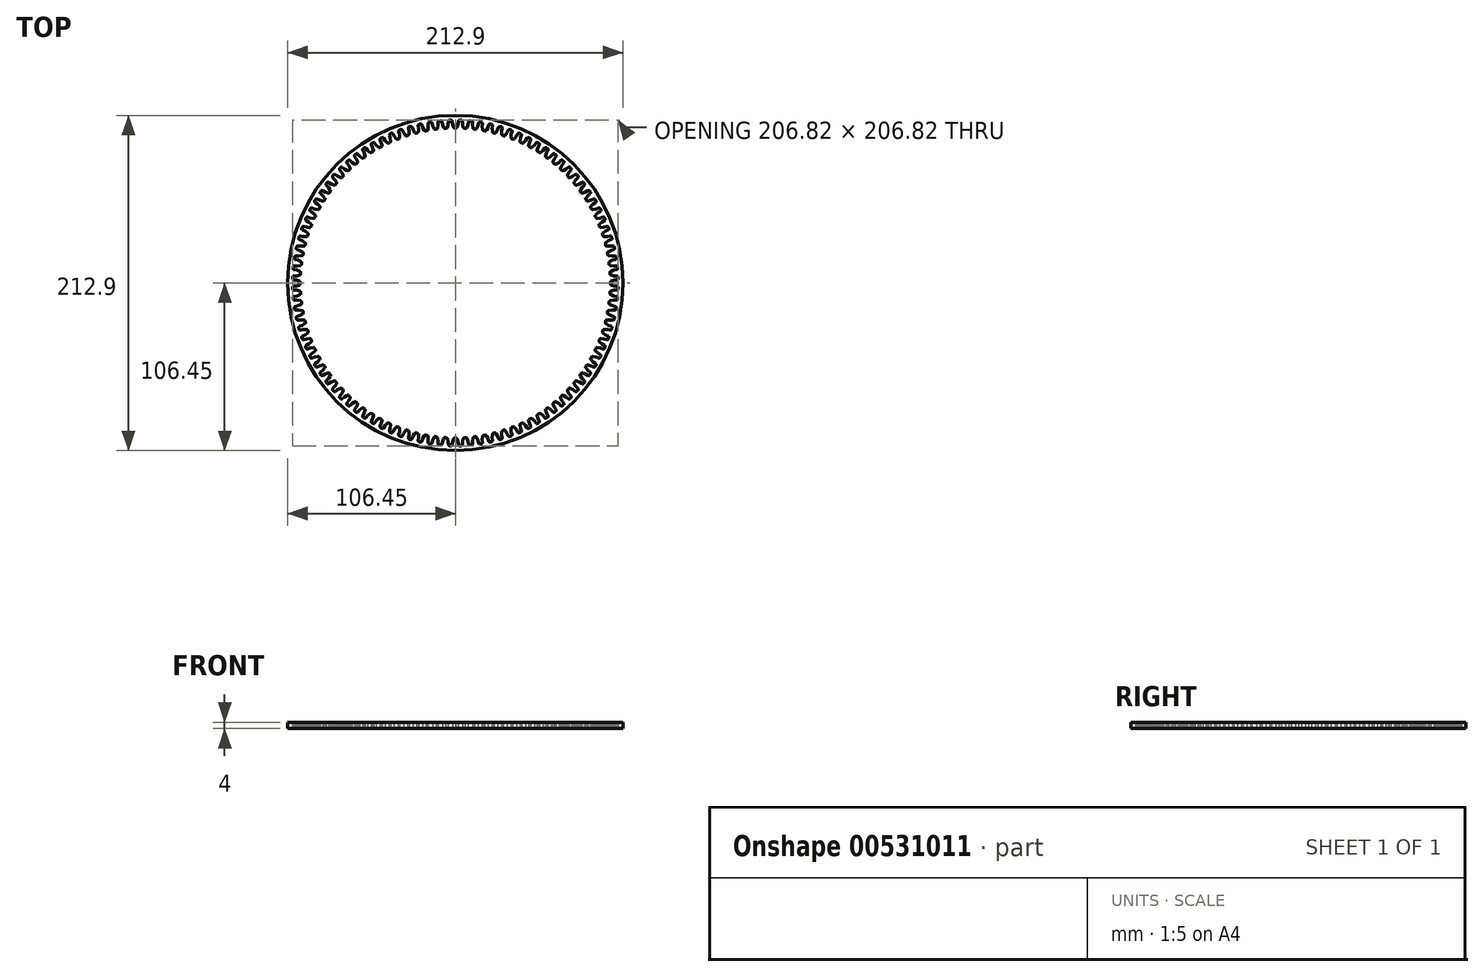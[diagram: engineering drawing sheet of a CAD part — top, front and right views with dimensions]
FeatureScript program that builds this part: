
annotation { "Feature Type Name" : "Feature", "Feature Type Description" : "" }
export const myFeature = defineFeature(function(context is Context, id is Id, definition is map)
    precondition{}
    {
        {
            assignVariable(context, id + "F0", {"name" : "debljina", "anyValue" : 4});
        }
        {
            assignVariable(context, id + "F1", {"name" : "nzuba", "anyValue" : 100});
        }
        {
            var Q0;
            Q0=qCreatedBy(makeId("Front.planeOp"),FACE);
            var sketch = newSketch(context, id + "F2", { "sketchPlane" : qUnion([Q0])});
            skLineSegment(sketch, "E0", {"start": v(0, 0) * mm, "end": v(0, 4) * mm, "construction": true});
            skSolve(sketch);
        }
        {
            var Q0;
            Q0=qCreatedBy(makeId("Top.planeOp"),FACE);
            var sketch = newSketch(context, id + "F3", { "sketchPlane" : qUnion([Q0])});
            skCircle(sketch, "E1", {"center": v(0, 0) * mm, "radius": 1.5 * mm});
            skCircle(sketch, "E2", {"center": v(0, 0) * mm, "radius": 98.45 * mm, "construction": true});
            skCircle(sketch, "E3", {"center": v(0, 0) * mm, "radius": 100.95 * mm, "construction": true});
            skLineSegment(sketch, "E4", {"start": v(0, 103.45) * mm, "end": v(0, 98.45) * mm, "construction": true});
            skLineSegment(sketch, "E5", {"start": v(-6.07, 103.27) * mm, "end": v(-5.92, 100.78) * mm});
            skLineSegment(sketch, "E6", {"start": v(-5.92, 100.78) * mm, "end": v(-5.78, 98.28) * mm});
            skCircle(sketch, "E7", {"center": v(0, 0) * mm, "radius": 106.45 * mm});
            skLineSegment(sketch, "E8", {"start": v(-106.45, 0) * mm, "end": v(0, 0) * mm, "construction": true});
            skLineSegment(sketch, "E9", {"start": v(-98.45, 0) * mm, "end": v(-98.45, 0.41) * mm});
            skLineSegment(sketch, "E10", {"start": v(-99, 1.18) * mm, "end": v(-100.93, 1.8) * mm});
            skLineSegment(sketch, "E11", {"start": v(-100.93, 1.8) * mm, "end": v(-102.62, 2) * mm});
            skLineSegment(sketch, "E12", {"start": v(-103.4, 3.25) * mm, "end": v(-103.4, 2.92) * mm});
            skArc(sketch, "E13", {"start": v(-103.4, 2.92) * mm, "mid": v(-103.2, 2.3) * mm, "end": v(-102.62, 2) * mm});
            skPoint(sketch, "E14.visualSharp", {"position": v(-98.45, 1) * mm});
            skArc(sketch, "E14.filletArc", {"start": v(-98.45, 0.41) * mm, "mid": v(-98.6, 0.89) * mm, "end": v(-99, 1.18) * mm});
            skLineSegment(sketch, "E15.MirrorCS", {"start": v(-98.45, 0) * mm, "end": v(-98.45, -0.41) * mm});
            skArc(sketch, "E16.MirrorCS", {"start": v(-98.45, -0.41) * mm, "mid": v(-98.6, -0.89) * mm, "end": v(-99, -1.18) * mm});
            skLineSegment(sketch, "E17.MirrorCS", {"start": v(-99, -1.18) * mm, "end": v(-100.93, -1.8) * mm});
            skLineSegment(sketch, "E18.MirrorCS", {"start": v(-100.93, -1.8) * mm, "end": v(-102.62, -2) * mm});
            skArc(sketch, "E19.MirrorCS", {"start": v(-103.4, -2.92) * mm, "mid": v(-103.2, -2.3) * mm, "end": v(-102.62, -2) * mm});
            skLineSegment(sketch, "E20.MirrorCS", {"start": v(-103.4, -3.25) * mm, "end": v(-103.4, -2.92) * mm});
            skLineSegment(sketch, "E21.MirrorCS", {"start": v(0, 0) * mm, "end": v(-1.5, -0.05) * mm});
            skArc(sketch, "E22", {"start": v(-103.4, -3.25) * mm, "mid": v(103.45, 0) * mm, "end": v(-103.4, 3.25) * mm});
            skArc(sketch, "E23", {"start": v(-2.5, 4.33) * mm, "mid": v(-4.33, 2.5) * mm, "end": v(-5, 0) * mm});
            skLineSegment(sketch, "E24", {"start": v(-2.5, 4.33) * mm, "end": v(-2.5, 103.42) * mm});
            skLineSegment(sketch, "E25", {"start": v(2.5, 4.33) * mm, "end": v(2.5, 103.42) * mm});
            skLineSegment(sketch, "E26", {"start": v(-2.5, 33.46) * mm, "end": v(2.5, 33.46) * mm});
            skLineSegment(sketch, "E27", {"start": v(0, 33.46) * mm, "end": v(0, 5) * mm});
            skLineSegment(sketch, "E28.1.0", {"start": v(-5, 0) * mm, "end": v(-90.81, -49.55) * mm});
            skLineSegment(sketch, "E28.1.1", {"start": v(-2.5, -4.33) * mm, "end": v(-88.31, -53.88) * mm});
            skLineSegment(sketch, "E28.2.0", {"start": v(2.5, -4.33) * mm, "end": v(88.31, -53.88) * mm});
            skLineSegment(sketch, "E28.2.1", {"start": v(5, 0) * mm, "end": v(90.81, -49.55) * mm});
            skArc(sketch, "E29.trimOffspring", {"start": v(5, 0) * mm, "mid": v(4.33, 2.5) * mm, "end": v(2.5, 4.33) * mm});
            skArc(sketch, "E30.trimOffspring", {"start": v(-2.5, -4.33) * mm, "mid": v(0, -5) * mm, "end": v(2.5, -4.33) * mm});
            skLineSegment(sketch, "E31.trimOffspring", {"start": v(-103.4, -3.25) * mm, "end": v(-106.4, -3.34) * mm});
            skLineSegment(sketch, "E32.trimOffspring", {"start": v(-103.4, 3.25) * mm, "end": v(-106.4, 3.34) * mm});
            skSolve(sketch);
        }
        {
            var Q0;
            Q0=makeQuery(id+"F3.imprint","IMPRINT",FACE,{"disambiguationData":[TD([[makeQuery(id+"F3.imprint","IMPRINT",EDGE,{"derivedFrom":sQuery(id+"F3.wireOp",EDGE,"E9")}),1.0]])]});
            extrude(context, id + "F4", {"entities" : qUnion([Q0]), "depth" : (getVariable(context, 'debljina')) * mm, "offsetDistance" : 25 * mm});
        }
        {
            var Q0;
            Q0=makeQuery(id+"F4.opExtrude","SWEPT_BODY",BODY,{"disambiguationData":[OSD([sQuery(id+"F3.wireOp",EDGE,"E7"),sQuery(id+"F3.wireOp",EDGE,"E9"),sQuery(id+"F3.wireOp",EDGE,"E10"),sQuery(id+"F3.wireOp",EDGE,"E11"),sQuery(id+"F3.wireOp",EDGE,"E12"),sQuery(id+"F3.wireOp",EDGE,"E13"),sQuery(id+"F3.wireOp",EDGE,"E14.filletArc"),sQuery(id+"F3.wireOp",EDGE,"E15.MirrorCS"),sQuery(id+"F3.wireOp",EDGE,"E16.MirrorCS"),sQuery(id+"F3.wireOp",EDGE,"E17.MirrorCS"),sQuery(id+"F3.wireOp",EDGE,"E18.MirrorCS"),sQuery(id+"F3.wireOp",EDGE,"E19.MirrorCS"),sQuery(id+"F3.wireOp",EDGE,"E20.MirrorCS"),sQuery(id+"F3.wireOp",EDGE,"E31.trimOffspring"),sQuery(id+"F3.wireOp",EDGE,"E32.trimOffspring")])]});
            var Q1;
            Q1=sQuery(id+"F2.wireOp",EDGE,"E0");
            circularPattern(context, id + "F5", {"operationType" : NewBodyOperationType.ADD, "entities" : qUnion([Q0]), "axis" : qUnion([Q1]), "angle" : 360 * degree, "instanceCount" : getVariable(context, 'nzuba'), "equalSpace" : true, "computeTransformsWithoutBuiltin" : true});
        }
    });
